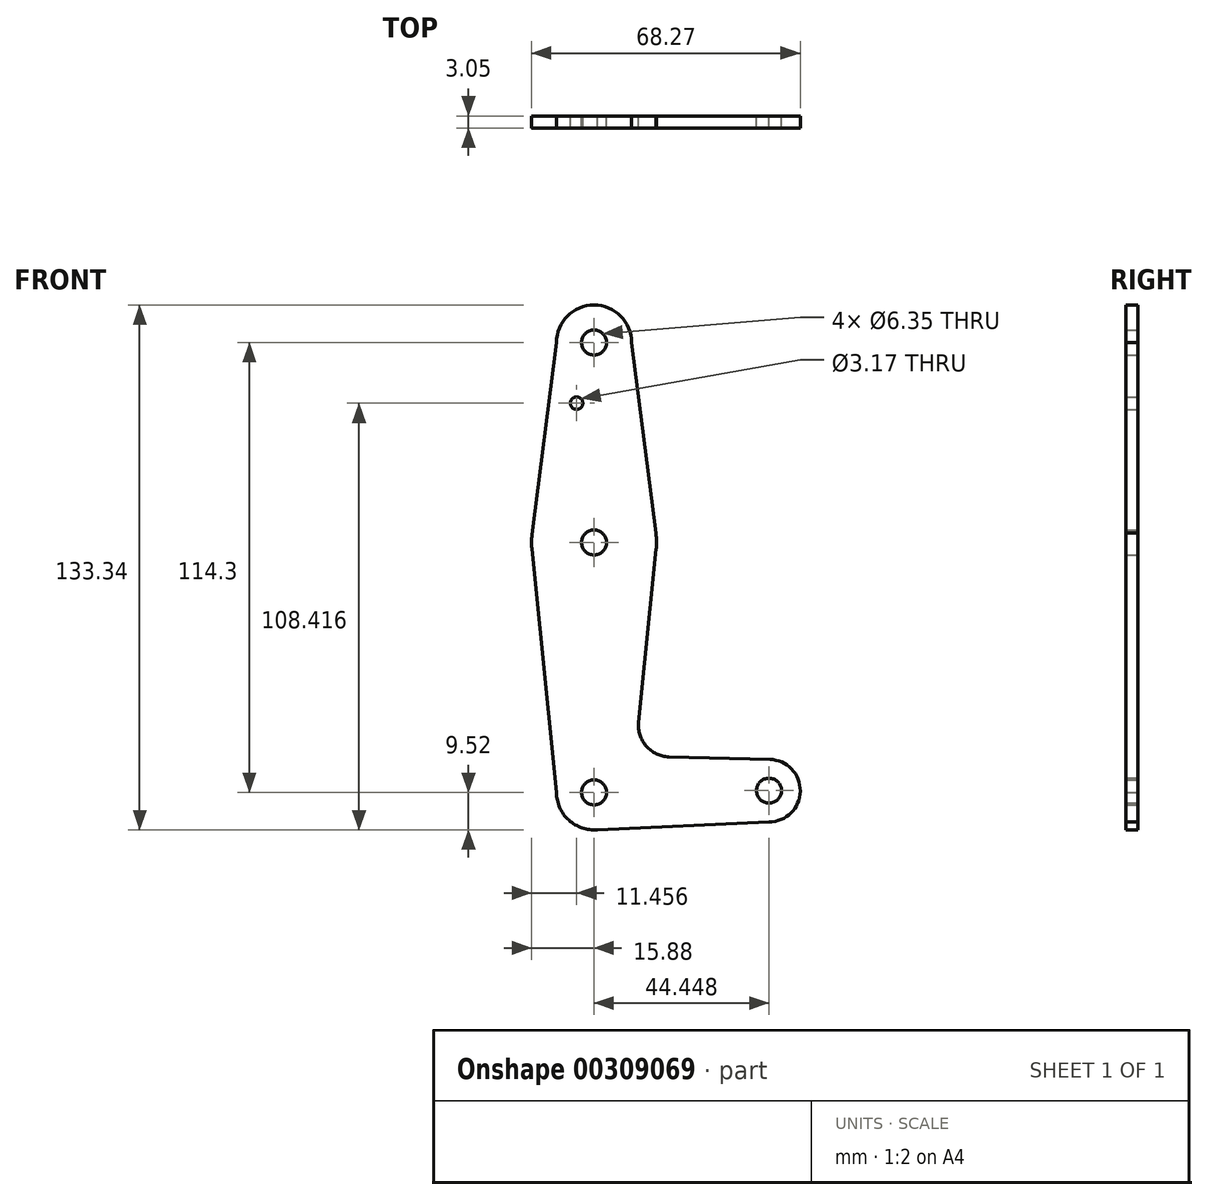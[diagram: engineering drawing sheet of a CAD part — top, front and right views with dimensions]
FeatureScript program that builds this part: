
annotation { "Feature Type Name" : "Feature", "Feature Type Description" : "" }
export const myFeature = defineFeature(function(context is Context, id is Id, definition is map)
    precondition{}
    {
        {
            var Q0;
            Q0=qCreatedBy(makeId("Front.planeOp"),FACE);
            var sketch = newSketch(context, id + "F0", { "sketchPlane" : qUnion([Q0])});
            skCircle(sketch, "E0", {"center": v(0, 0) * mm, "radius": 15.88 * mm});
            skCircle(sketch, "E1", {"center": v(0, 50.8) * mm, "radius": 9.53 * mm});
            skCircle(sketch, "E2", {"center": v(0, -63.5) * mm, "radius": 9.53 * mm});
            skCircle(sketch, "E3", {"center": v(44.45, -63.06) * mm, "radius": 7.94 * mm});
            skLineSegment(sketch, "E4", {"start": v(44.65, -55.12) * mm, "end": v(19.03, -54.46) * mm});
            skLineSegment(sketch, "E5", {"start": v(0, -73.03) * mm, "end": v(44.45, -71) * mm});
            skLineSegment(sketch, "E6", {"start": v(44.45, -71) * mm, "end": v(0, -73.03) * mm});
            skLineSegment(sketch, "E7", {"start": v(-9.53, -63.5) * mm, "end": v(-15.8, -1.6) * mm});
            skLineSegment(sketch, "E8", {"start": v(-15.8, -1.6) * mm, "end": v(-9.53, -63.5) * mm});
            skLineSegment(sketch, "E9", {"start": v(11.33, -45.72) * mm, "end": v(15.8, -1.6) * mm});
            skLineSegment(sketch, "E10", {"start": v(-9.52, 50.8) * mm, "end": v(-15.8, 1.64) * mm});
            skLineSegment(sketch, "E11", {"start": v(-15.8, 1.64) * mm, "end": v(-9.52, 50.8) * mm});
            skLineSegment(sketch, "E12", {"start": v(9.53, 50.8) * mm, "end": v(15.79, 1.64) * mm});
            skLineSegment(sketch, "E13", {"start": v(15.79, 1.64) * mm, "end": v(9.53, 50.8) * mm});
            skArc(sketch, "E14.filletArc", {"start": v(11.33, -45.72) * mm, "mid": v(13.27, -51.77) * mm, "end": v(19.03, -54.46) * mm});
            skCircle(sketch, "E15", {"center": v(-4.42, 35.4) * mm, "radius": 1.59 * mm});
            skCircle(sketch, "E16", {"center": v(0, 50.8) * mm, "radius": 3.18 * mm});
            skCircle(sketch, "E17", {"center": v(0, 0) * mm, "radius": 3.18 * mm});
            skCircle(sketch, "E18", {"center": v(0, -63.5) * mm, "radius": 3.18 * mm});
            skCircle(sketch, "E19", {"center": v(44.45, -63.06) * mm, "radius": 3.18 * mm});
            skSolve(sketch);
        }
        {
            var Q0;
            Q0 = qSketchRegion(id + "F0", true);
            extrude(context, id + "F1", {"entities" : qUnion([Q0]), "depth" : 3.05 * mm});
        }
    });
